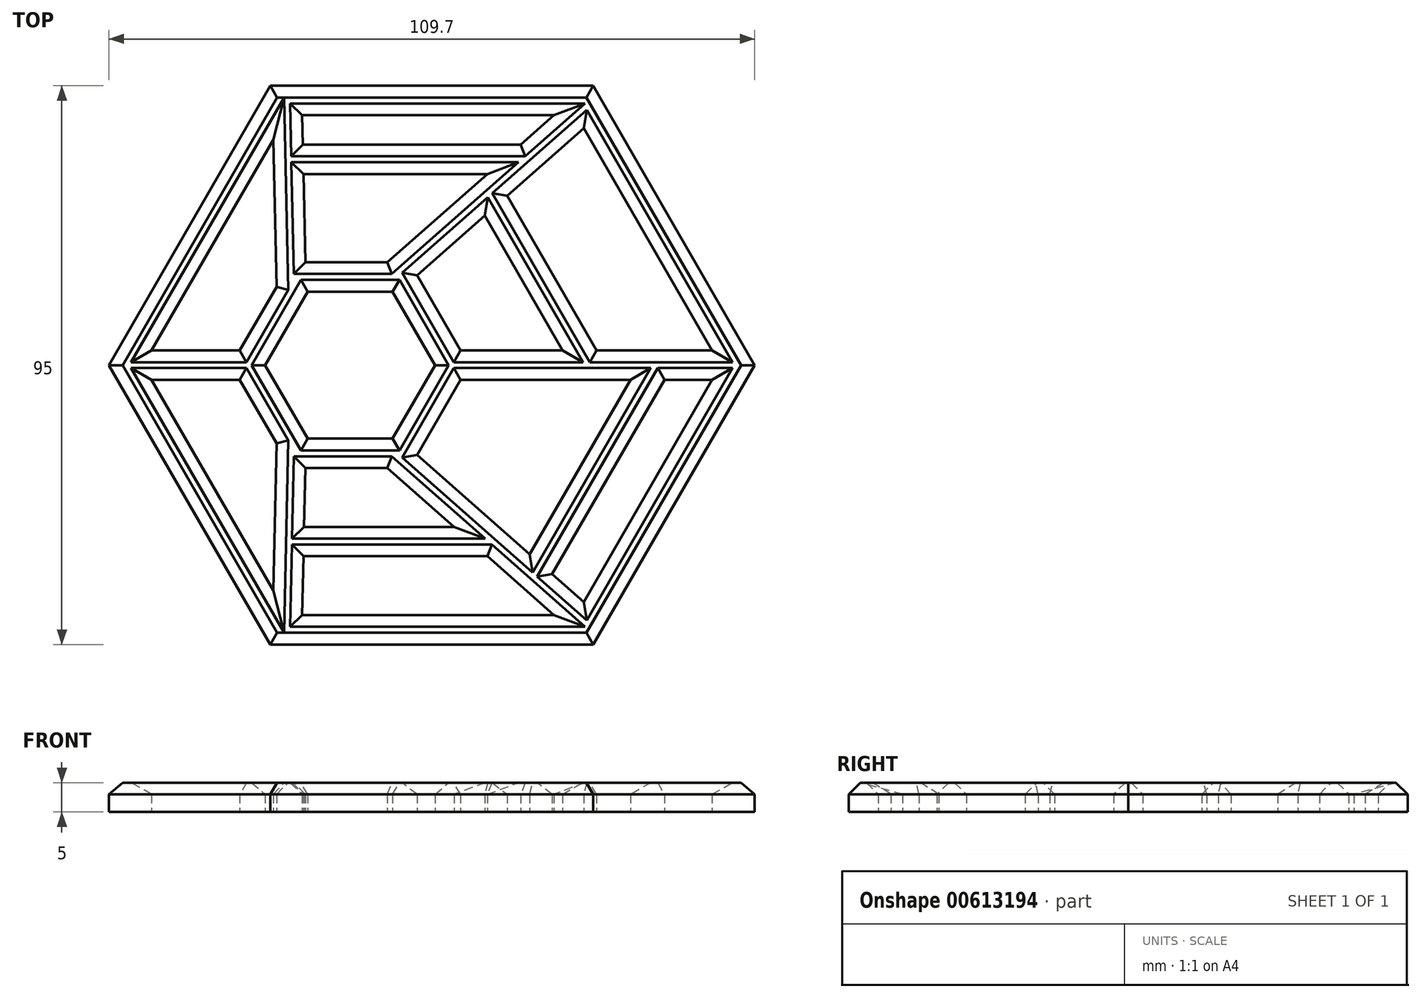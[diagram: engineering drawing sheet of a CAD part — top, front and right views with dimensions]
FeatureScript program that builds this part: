
annotation { "Feature Type Name" : "Feature", "Feature Type Description" : "" }
export const myFeature = defineFeature(function(context is Context, id is Id, definition is map)
    precondition{}
    {
        {
            var Q0;
            Q0=qCreatedBy(makeId("Top.planeOp"),FACE);
            var sketch = newSketch(context, id + "F0", { "sketchPlane" : qUnion([Q0])});
            skCircle(sketch, "E0.cCircle", {"center": v(0, 0) * mm, "radius": 47.5 * mm, "construction": true});
            skLineSegment(sketch, "E0.0", {"start": v(-27.42, 47.5) * mm, "end": v(27.42, 47.5) * mm});
            skLineSegment(sketch, "E0.1", {"start": v(27.42, 47.5) * mm, "end": v(54.85, 0) * mm});
            skLineSegment(sketch, "E0.2", {"start": v(54.85, 0) * mm, "end": v(27.42, -47.5) * mm});
            skLineSegment(sketch, "E0.3", {"start": v(27.42, -47.5) * mm, "end": v(-27.42, -47.5) * mm});
            skLineSegment(sketch, "E0.4", {"start": v(-27.42, -47.5) * mm, "end": v(-54.85, 0) * mm});
            skLineSegment(sketch, "E0.5", {"start": v(-54.85, 0) * mm, "end": v(-27.42, 47.5) * mm});
            skPoint(sketch, "E0.0.midPoint", {"position": v(0, 47.5) * mm});
            skLineSegment(sketch, "E1.0", {"start": v(-49.07, 0) * mm, "end": v(-24.54, 42.5) * mm});
            skLineSegment(sketch, "E1.1", {"start": v(24.54, 42.5) * mm, "end": v(49.07, 0) * mm});
            skLineSegment(sketch, "E1.2", {"start": v(49.07, 0) * mm, "end": v(24.54, -42.5) * mm});
            skLineSegment(sketch, "E1.3", {"start": v(-24.54, 42.5) * mm, "end": v(24.54, 42.5) * mm});
            skLineSegment(sketch, "E1.4", {"start": v(24.54, -42.5) * mm, "end": v(-24.54, -42.5) * mm});
            skLineSegment(sketch, "E1.5", {"start": v(-24.54, -42.5) * mm, "end": v(-49.07, 0) * mm});
            skLineSegment(sketch, "E2", {"start": v(-49.07, 0) * mm, "end": v(0, 0) * mm, "construction": true});
            skCircle(sketch, "E3.cCircle", {"center": v(-13.87, 0) * mm, "radius": 17.5 * mm, "construction": true});
            skLineSegment(sketch, "E3.0", {"start": v(-23.97, 17.5) * mm, "end": v(-3.76, 17.5) * mm});
            skLineSegment(sketch, "E3.1", {"start": v(-3.76, 17.5) * mm, "end": v(6.34, 0) * mm});
            skLineSegment(sketch, "E3.2", {"start": v(6.34, 0) * mm, "end": v(-3.76, -17.5) * mm});
            skLineSegment(sketch, "E3.3", {"start": v(-3.76, -17.5) * mm, "end": v(-23.97, -17.5) * mm});
            skLineSegment(sketch, "E3.4", {"start": v(-23.97, -17.5) * mm, "end": v(-34.07, 0) * mm});
            skLineSegment(sketch, "E3.5", {"start": v(-34.07, 0) * mm, "end": v(-23.97, 17.5) * mm});
            skPoint(sketch, "E3.0.midPoint", {"position": v(-13.87, 17.5) * mm});
            skLineSegment(sketch, "E4.0", {"start": v(-28.3, 0) * mm, "end": v(-21.08, 12.5) * mm});
            skLineSegment(sketch, "E4.1", {"start": v(-6.65, 12.5) * mm, "end": v(0.57, 0) * mm});
            skLineSegment(sketch, "E4.2", {"start": v(0.57, 0) * mm, "end": v(-6.65, -12.5) * mm});
            skLineSegment(sketch, "E4.3", {"start": v(-21.08, 12.5) * mm, "end": v(-6.65, 12.5) * mm});
            skLineSegment(sketch, "E4.4", {"start": v(-6.65, -12.5) * mm, "end": v(-21.08, -12.5) * mm});
            skLineSegment(sketch, "E4.5", {"start": v(-21.08, -12.5) * mm, "end": v(-28.3, 0) * mm});
            skLineSegment(sketch, "E5", {"start": v(6.34, 0) * mm, "end": v(49.07, 0) * mm});
            skLineSegment(sketch, "E6", {"start": v(-3.76, -17.5) * mm, "end": v(24.54, -42.5) * mm});
            skLineSegment(sketch, "E7", {"start": v(-23.97, -17.5) * mm, "end": v(-24.54, -42.5) * mm});
            skLineSegment(sketch, "E8", {"start": v(-34.07, 0) * mm, "end": v(-49.07, 0) * mm});
            skLineSegment(sketch, "E9", {"start": v(-3.76, 17.5) * mm, "end": v(24.54, 42.5) * mm});
            skLineSegment(sketch, "E10", {"start": v(-23.97, 17.5) * mm, "end": v(-24.54, 42.5) * mm});
            skLineSegment(sketch, "E11.0", {"start": v(-21.47, 17.5) * mm, "end": v(-22.04, 42.5) * mm});
            skLineSegment(sketch, "E12.0", {"start": v(-26.38, 13.33) * mm, "end": v(-26.94, 38.33) * mm});
            skLineSegment(sketch, "E13.0", {"start": v(-2.49, 15.3) * mm, "end": v(25.81, 40.3) * mm});
            skLineSegment(sketch, "E14.0", {"start": v(-7.54, 17.5) * mm, "end": v(20.76, 42.5) * mm});
            skLineSegment(sketch, "E15.0", {"start": v(4.9, -2.5) * mm, "end": v(47.63, -2.5) * mm});
            skLineSegment(sketch, "E16.0", {"start": v(4.9, 2.5) * mm, "end": v(47.63, 2.5) * mm});
            skLineSegment(sketch, "E17.0", {"start": v(-7.54, -17.5) * mm, "end": v(20.76, -42.5) * mm});
            skLineSegment(sketch, "E18.0", {"start": v(-2.49, -15.3) * mm, "end": v(25.81, -40.3) * mm});
            skLineSegment(sketch, "E19.0", {"start": v(-26.38, -13.33) * mm, "end": v(-26.94, -38.33) * mm});
            skLineSegment(sketch, "E20.0", {"start": v(-21.47, -17.5) * mm, "end": v(-22.04, -42.5) * mm});
            skLineSegment(sketch, "E21.0", {"start": v(-47.63, -2.5) * mm, "end": v(-32.63, -2.5) * mm});
            skLineSegment(sketch, "E22.0", {"start": v(-47.63, 2.5) * mm, "end": v(-32.63, 2.5) * mm});
            skLineSegment(sketch, "E23.0", {"start": v(8.98, 25.42) * mm, "end": v(22.22, 2.5) * mm});
            skLineSegment(sketch, "E24.0", {"start": v(12.8, 28.8) * mm, "end": v(28, 2.5) * mm});
            skLineSegment(sketch, "E25.0", {"start": v(33.76, -2.5) * mm, "end": v(16.63, -32.18) * mm});
            skLineSegment(sketch, "E26.0", {"start": v(39.54, -2.5) * mm, "end": v(20.45, -35.56) * mm});
            skLineSegment(sketch, "E27.0", {"start": v(3.78, -27.5) * mm, "end": v(-21.7, -27.5) * mm});
            skLineSegment(sketch, "E28.0", {"start": v(9.44, -32.5) * mm, "end": v(-21.81, -32.5) * mm});
            skLineSegment(sketch, "E29.0", {"start": v(-21.92, 37.5) * mm, "end": v(15.1, 37.5) * mm});
            skLineSegment(sketch, "E30.0", {"start": v(-21.81, 32.5) * mm, "end": v(9.44, 32.5) * mm});
            skSolve(sketch);
        }
        {
            var Q0;
            Q0=makeQuery(id+"F0.imprint","IMPRINT",FACE,{"disambiguationData":[TD([[makeQuery(id+"F0.imprint","IMPRINT",EDGE,{"derivedFrom":sQuery(id+"F0.wireOp",EDGE,"E4.0")}),1.0]])]});
            var Q1;
            {var subQ0=sQuery(id+"F0.wireOp",EDGE,"E10");Q1=makeQuery(id+"F0.imprint","IMPRINT",FACE,{"disambiguationData":[TD([[makeQuery(id+"F0.imprint","IMPRINT",EDGE,{"derivedFrom":subQ0}),-1.0]])]});}
            var Q2;
            {var subQ0=sQuery(id+"F0.wireOp",EDGE,"E8");Q2=makeQuery(id+"F0.imprint","IMPRINT",FACE,{"disambiguationData":[TD([[makeQuery(id+"F0.imprint","IMPRINT",EDGE,{"derivedFrom":subQ0}),-1.0]])]});}
            var Q3;
            Q3=makeQuery(id+"F0.imprint","IMPRINT",FACE,{"disambiguationData":[TD([[makeQuery(id+"F0.imprint","IMPRINT",EDGE,{"derivedFrom":sQuery(id+"F0.wireOp",EDGE,"E0.0")}),-1.0]])]});
            var Q4;
            {var subQ0=sQuery(id+"F0.wireOp",EDGE,"E7");Q4=makeQuery(id+"F0.imprint","IMPRINT",FACE,{"disambiguationData":[TD([[makeQuery(id+"F0.imprint","IMPRINT",EDGE,{"derivedFrom":subQ0}),1.0]])]});}
            var Q5;
            {var subQ0=sQuery(id+"F0.wireOp",EDGE,"E6");Q5=makeQuery(id+"F0.imprint","IMPRINT",FACE,{"disambiguationData":[TD([[makeQuery(id+"F0.imprint","IMPRINT",EDGE,{"derivedFrom":subQ0}),-1.0]])]});}
            var Q6;
            {var subQ0=sQuery(id+"F0.wireOp",EDGE,"E5");Q6=makeQuery(id+"F0.imprint","IMPRINT",FACE,{"disambiguationData":[TD([[makeQuery(id+"F0.imprint","IMPRINT",EDGE,{"derivedFrom":subQ0}),-1.0]])]});}
            var Q7;
            {var subQ0=sQuery(id+"F0.wireOp",EDGE,"E9");Q7=makeQuery(id+"F0.imprint","IMPRINT",FACE,{"disambiguationData":[TD([[makeQuery(id+"F0.imprint","IMPRINT",EDGE,{"derivedFrom":subQ0}),-1.0]])]});}
            var Q8;
            {var subQ0=sQuery(id+"F0.wireOp",EDGE,"E10");Q8=makeQuery(id+"F0.imprint","IMPRINT",FACE,{"disambiguationData":[TD([[makeQuery(id+"F0.imprint","IMPRINT",EDGE,{"derivedFrom":subQ0}),1.0]])]});}
            var Q9;
            {var subQ0=sQuery(id+"F0.wireOp",EDGE,"E8");Q9=makeQuery(id+"F0.imprint","IMPRINT",FACE,{"disambiguationData":[TD([[makeQuery(id+"F0.imprint","IMPRINT",EDGE,{"derivedFrom":subQ0}),1.0]])]});}
            var Q10;
            {var subQ0=sQuery(id+"F0.wireOp",EDGE,"E7");Q10=makeQuery(id+"F0.imprint","IMPRINT",FACE,{"disambiguationData":[TD([[makeQuery(id+"F0.imprint","IMPRINT",EDGE,{"derivedFrom":subQ0}),-1.0]])]});}
            var Q11;
            {var subQ0=sQuery(id+"F0.wireOp",EDGE,"E5");Q11=makeQuery(id+"F0.imprint","IMPRINT",FACE,{"disambiguationData":[TD([[makeQuery(id+"F0.imprint","IMPRINT",EDGE,{"derivedFrom":subQ0}),1.0]])]});}
            var Q12;
            {var subQ0=sQuery(id+"F0.wireOp",EDGE,"E9");Q12=makeQuery(id+"F0.imprint","IMPRINT",FACE,{"disambiguationData":[TD([[makeQuery(id+"F0.imprint","IMPRINT",EDGE,{"derivedFrom":subQ0}),1.0]])]});}
            var Q13;
            {var subQ0=sQuery(id+"F0.wireOp",EDGE,"E6");Q13=makeQuery(id+"F0.imprint","IMPRINT",FACE,{"disambiguationData":[TD([[makeQuery(id+"F0.imprint","IMPRINT",EDGE,{"derivedFrom":subQ0}),1.0]])]});}
            var Q14;
            {var subQ0=sQuery(id+"F0.wireOp",EDGE,"E23.0");Q14=makeQuery(id+"F0.imprint","IMPRINT",FACE,{"disambiguationData":[TD([[makeQuery(id+"F0.imprint","IMPRINT",EDGE,{"derivedFrom":subQ0}),1.0]])]});}
            var Q15;
            {var subQ0=sQuery(id+"F0.wireOp",EDGE,"E25.0");Q15=makeQuery(id+"F0.imprint","IMPRINT",FACE,{"disambiguationData":[TD([[makeQuery(id+"F0.imprint","IMPRINT",EDGE,{"derivedFrom":subQ0}),1.0]])]});}
            var Q16;
            {var subQ0=sQuery(id+"F0.wireOp",EDGE,"E27.0");Q16=makeQuery(id+"F0.imprint","IMPRINT",FACE,{"disambiguationData":[TD([[makeQuery(id+"F0.imprint","IMPRINT",EDGE,{"derivedFrom":subQ0}),1.0]])]});}
            var Q17;
            {var subQ0=sQuery(id+"F0.wireOp",EDGE,"E29.0");Q17=makeQuery(id+"F0.imprint","IMPRINT",FACE,{"disambiguationData":[TD([[makeQuery(id+"F0.imprint","IMPRINT",EDGE,{"derivedFrom":subQ0}),-1.0]])]});}
            extrude(context, id + "F1", {"entities" : qUnion([Q0, Q1, Q2, Q3, Q4, Q5, Q6, Q7, Q8, Q9, Q10, Q11, Q12, Q13, Q14, Q15, Q16, Q17]), "depth" : 5 * mm, "offsetDistance" : 25 * mm});
        }
        {
            var Q0;
            Q0=makeQuery(id+"F1.opExtrude","CAP_FACE",FACE,{"disambiguationData":[OSD([sQuery(id+"F0.wireOp",EDGE,"E0.0"),sQuery(id+"F0.wireOp",EDGE,"E0.1"),sQuery(id+"F0.wireOp",EDGE,"E0.2"),sQuery(id+"F0.wireOp",EDGE,"E0.3"),sQuery(id+"F0.wireOp",EDGE,"E0.4"),sQuery(id+"F0.wireOp",EDGE,"E0.5"),sQuery(id+"F0.wireOp",EDGE,"E1.0"),sQuery(id+"F0.wireOp",EDGE,"E1.1"),sQuery(id+"F0.wireOp",EDGE,"E1.2"),sQuery(id+"F0.wireOp",EDGE,"E1.3"),sQuery(id+"F0.wireOp",EDGE,"E1.4"),sQuery(id+"F0.wireOp",EDGE,"E1.5"),sQuery(id+"F0.wireOp",EDGE,"E3.0"),sQuery(id+"F0.wireOp",EDGE,"E3.1"),sQuery(id+"F0.wireOp",EDGE,"E3.2"),sQuery(id+"F0.wireOp",EDGE,"E3.3"),sQuery(id+"F0.wireOp",EDGE,"E3.4"),sQuery(id+"F0.wireOp",EDGE,"E3.5"),sQuery(id+"F0.wireOp",EDGE,"E4.0"),sQuery(id+"F0.wireOp",EDGE,"E4.1"),sQuery(id+"F0.wireOp",EDGE,"E4.2"),sQuery(id+"F0.wireOp",EDGE,"E4.3"),sQuery(id+"F0.wireOp",EDGE,"E4.4"),sQuery(id+"F0.wireOp",EDGE,"E4.5"),sQuery(id+"F0.wireOp",EDGE,"E11.0"),sQuery(id+"F0.wireOp",EDGE,"E12.0"),sQuery(id+"F0.wireOp",EDGE,"E13.0"),sQuery(id+"F0.wireOp",EDGE,"E14.0"),sQuery(id+"F0.wireOp",EDGE,"E15.0"),sQuery(id+"F0.wireOp",EDGE,"E16.0"),sQuery(id+"F0.wireOp",EDGE,"E17.0"),sQuery(id+"F0.wireOp",EDGE,"E18.0"),sQuery(id+"F0.wireOp",EDGE,"E19.0"),sQuery(id+"F0.wireOp",EDGE,"E20.0"),sQuery(id+"F0.wireOp",EDGE,"E21.0"),sQuery(id+"F0.wireOp",EDGE,"E22.0")])],"isStart":false});
            chamfer(context, id + "F2", {"entities" : qUnion([Q0]), "width" : 2 * mm, "tangentPropagation" : true});
        }
    });
